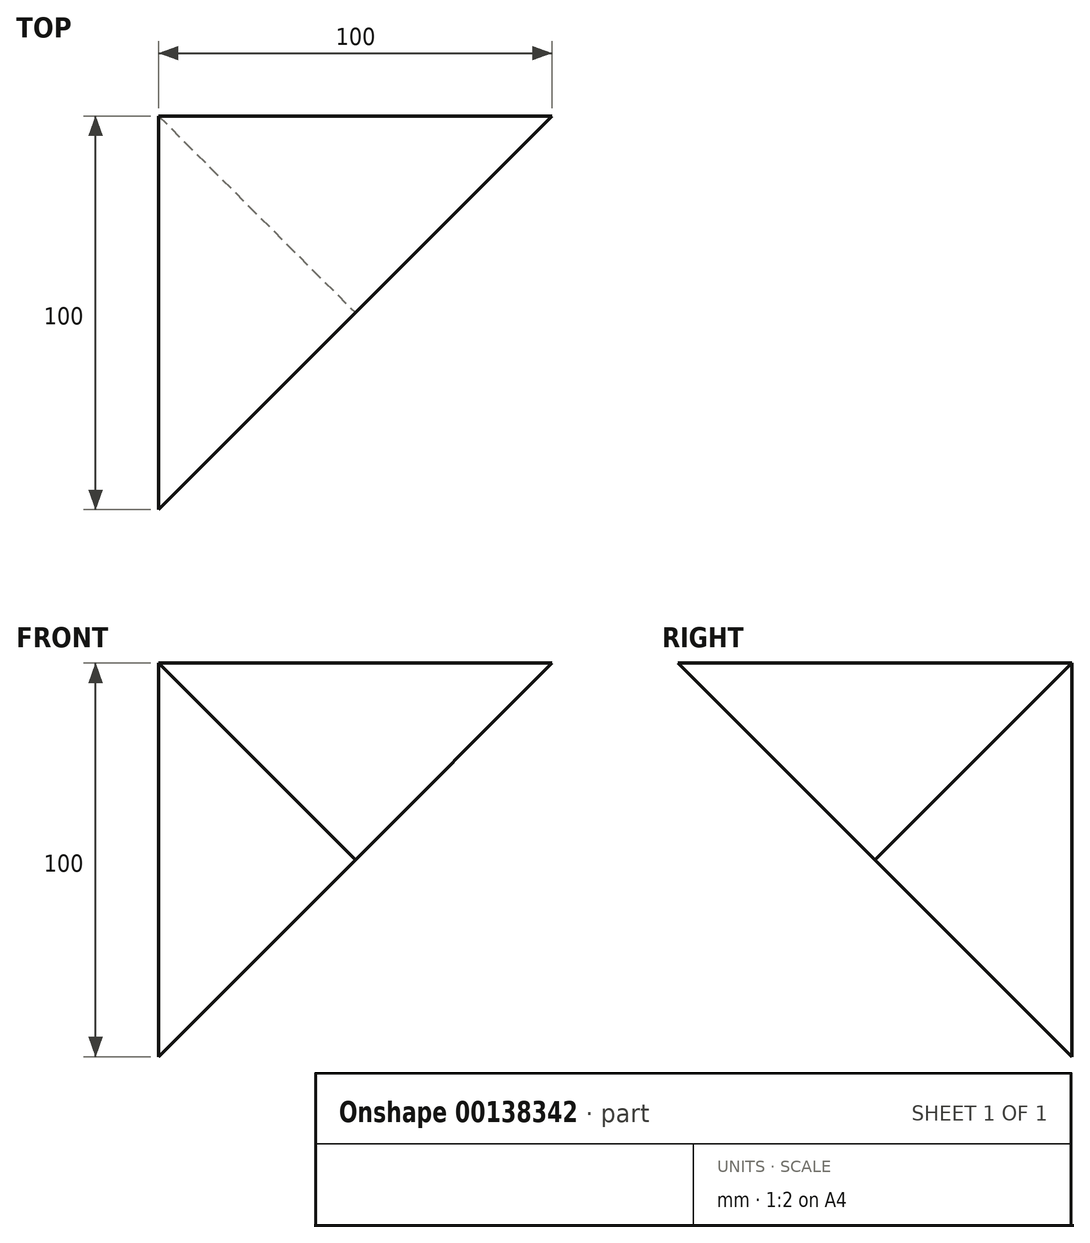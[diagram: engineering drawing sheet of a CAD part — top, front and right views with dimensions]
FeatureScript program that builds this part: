
annotation { "Feature Type Name" : "Feature", "Feature Type Description" : "" }
export const myFeature = defineFeature(function(context is Context, id is Id, definition is map)
    precondition{}
    {
        {
            var Q0;
            Q0=qCreatedBy(makeId("Front.planeOp"),FACE);
            var sketch = newSketch(context, id + "F0", { "sketchPlane" : qUnion([Q0])});
            skLineSegment(sketch, "E0.bottom", {"start": v(-43, 40.23) * mm, "end": v(57, 40.23) * mm});
            skLineSegment(sketch, "E0.top", {"start": v(-43, -59.77) * mm, "end": v(57, -59.77) * mm});
            skLineSegment(sketch, "E0.left", {"start": v(-43, 40.23) * mm, "end": v(-43, -59.77) * mm});
            skLineSegment(sketch, "E0.right", {"start": v(57, 40.23) * mm, "end": v(57, -59.77) * mm});
            skSolve(sketch);
        }
        {
            var Q0;
            Q0 = qSketchRegion(id + "F0", true);
            extrude(context, id + "F1", {"entities" : qUnion([Q0]), "depth" : 100 * mm});
        }
        {
            var Q0;
            Q0=makeQuery(id+"F1.opExtrude","SWEPT_FACE",FACE,{"disambiguationData":[OSD([sQuery(id+"F0.wireOp",EDGE,"E0.bottom")])]});
            var sketch = newSketch(context, id + "F2", { "sketchPlane" : qUnion([Q0])});
            skLineSegment(sketch, "E1", {"start": v(-43, -100) * mm, "end": v(57, 0) * mm});
            skLineSegment(sketch, "E2", {"start": v(57, 0) * mm, "end": v(57, -100) * mm});
            skLineSegment(sketch, "E3", {"start": v(57, -100) * mm, "end": v(-43, -100) * mm});
            skSolve(sketch);
        }
        {
            var Q0;
            Q0 = qSketchRegion(id + "F2", true);
            extrude(context, id + "F3", {"entities" : qUnion([Q0]), "operationType" : NewBodyOperationType.REMOVE, "oppositeDirection" : true, "depth" : 100 * mm});
        }
        {
            var Q0;
            Q0=makeQuery(id+"F1.opExtrude","SWEPT_FACE",FACE,{"disambiguationData":[OSD([sQuery(id+"F0.wireOp",EDGE,"E0.left")])]});
            var sketch = newSketch(context, id + "F4", { "sketchPlane" : qUnion([Q0])});
            skLineSegment(sketch, "E4", {"start": v(100, 40.23) * mm, "end": v(0, -59.77) * mm});
            skLineSegment(sketch, "E5", {"start": v(0, -59.77) * mm, "end": v(100, -59.77) * mm});
            skLineSegment(sketch, "E6", {"start": v(100, -59.77) * mm, "end": v(100, 40.23) * mm});
            skSolve(sketch);
        }
        {
            var Q0;
            Q0 = qSketchRegion(id + "F4", true);
            extrude(context, id + "F5", {"entities" : qUnion([Q0]), "operationType" : NewBodyOperationType.REMOVE, "oppositeDirection" : true, "depth" : 100 * mm});
        }
        {
            var Q0;
            Q0=makeQuery(id+"F1.opExtrude","CAP_FACE",FACE,{"disambiguationData":[OSD([sQuery(id+"F0.wireOp",EDGE,"E0.bottom"),sQuery(id+"F0.wireOp",EDGE,"E0.top"),sQuery(id+"F0.wireOp",EDGE,"E0.left"),sQuery(id+"F0.wireOp",EDGE,"E0.right")])],"isStart":true});
            var sketch = newSketch(context, id + "F6", { "sketchPlane" : qUnion([Q0])});
            skLineSegment(sketch, "E7", {"start": v(43, -59.77) * mm, "end": v(-57, 40.23) * mm});
            skLineSegment(sketch, "E8", {"start": v(-57, 40.23) * mm, "end": v(-57, -59.77) * mm});
            skLineSegment(sketch, "E9", {"start": v(43, -59.77) * mm, "end": v(-57, -59.77) * mm});
            skSolve(sketch);
        }
        {
            var Q0;
            Q0 = qSketchRegion(id + "F6", true);
            extrude(context, id + "F7", {"entities" : qUnion([Q0]), "operationType" : NewBodyOperationType.REMOVE, "oppositeDirection" : true, "depth" : 100 * mm});
        }
    });
